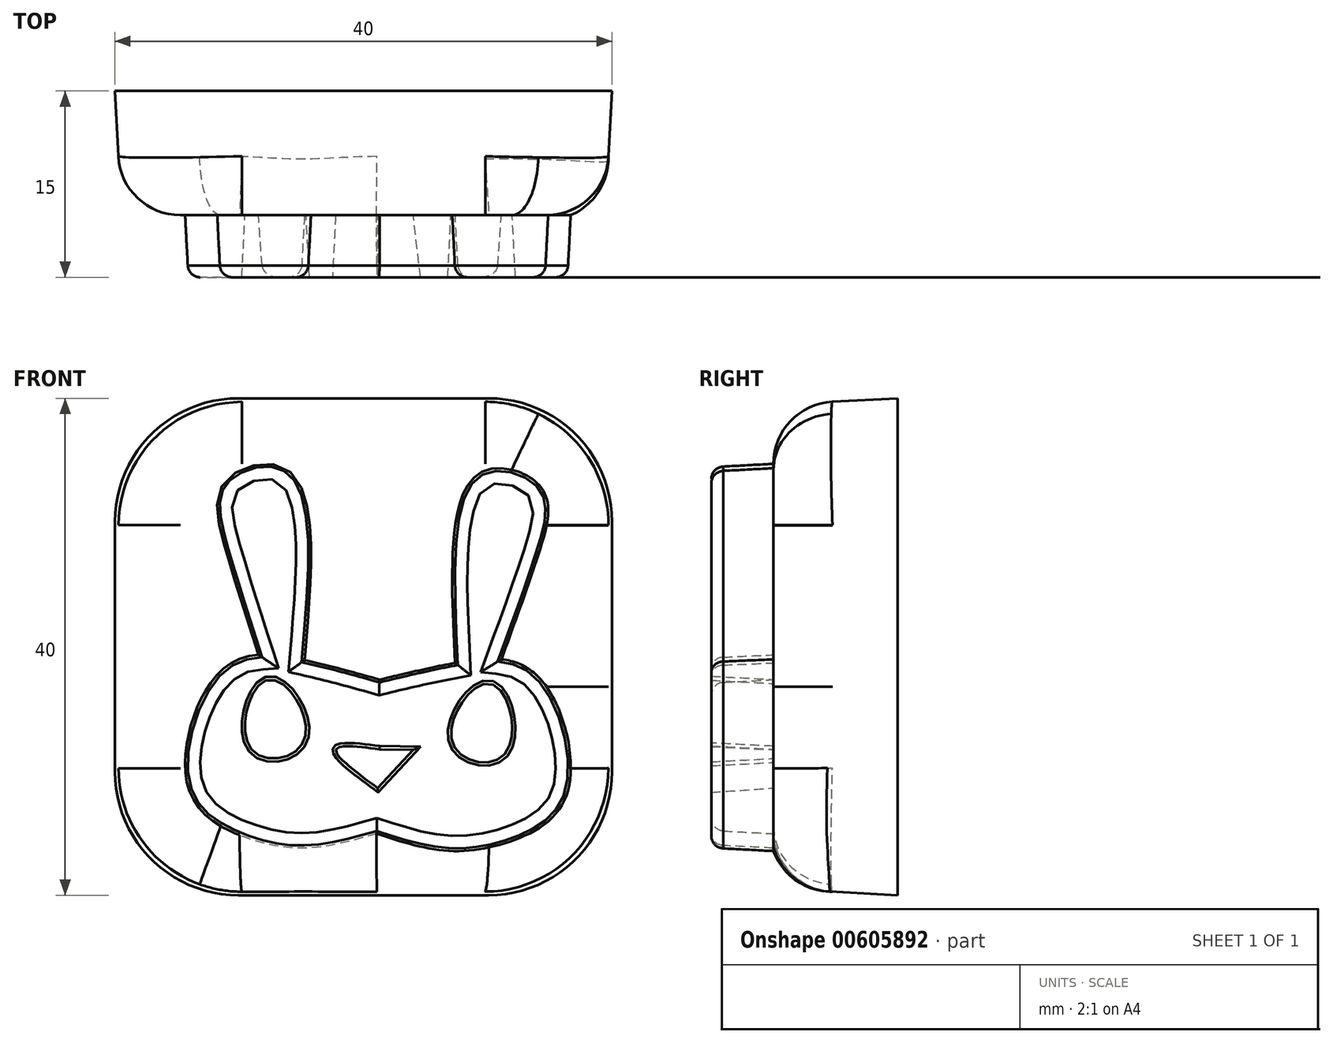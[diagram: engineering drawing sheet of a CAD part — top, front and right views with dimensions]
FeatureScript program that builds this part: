
annotation { "Feature Type Name" : "Feature", "Feature Type Description" : "" }
export const myFeature = defineFeature(function(context is Context, id is Id, definition is map)
    precondition{}
    {
        {
            var Q0;
            Q0=qCreatedBy(makeId("Front.planeOp"),FACE);
            var sketch = newSketch(context, id + "F0", { "sketchPlane" : qUnion([Q0])});
            skLineSegment(sketch, "E0.bottom", {"start": v(-5.85, 16.71) * mm, "end": v(34.15, 16.71) * mm});
            skLineSegment(sketch, "E0.top", {"start": v(-5.85, -23.29) * mm, "end": v(34.15, -23.29) * mm});
            skLineSegment(sketch, "E0.left", {"start": v(-5.85, 16.71) * mm, "end": v(-5.85, -23.29) * mm});
            skLineSegment(sketch, "E0.right", {"start": v(34.15, 16.71) * mm, "end": v(34.15, -23.29) * mm});
            skSolve(sketch);
        }
        {
            var Q0;
            Q0=makeQuery(id+"F0.imprint","IMPRINT",FACE,{"disambiguationData":[TD([[makeQuery(id+"F0.imprint","IMPRINT",EDGE,{"derivedFrom":sQuery(id+"F0.wireOp",EDGE,"E0.bottom")}),-1.0]])]});
            extrude(context, id + "F1", {"entities" : qUnion([Q0]), "depth" : 10 * mm, "offsetDistance" : 25 * mm, "hasDraft" : true, "draftAngle" : 3 * degree, "draftPullDirection" : true});
        }
        {
            var Q0;
            Q0=makeQuery(id+"F1.opExtrude","CAP_FACE",FACE,{"disambiguationData":[OSD([sQuery(id+"F0.wireOp",EDGE,"E0.bottom"),sQuery(id+"F0.wireOp",EDGE,"E0.top"),sQuery(id+"F0.wireOp",EDGE,"E0.left"),sQuery(id+"F0.wireOp",EDGE,"E0.right")])],"isStart":false});
            var sketch = newSketch(context, id + "F2", { "sketchPlane" : qUnion([Q0])});
            skFitSpline(sketch, "E1", {"points": [v(15.44, -5.94) * mm, v(9.4, -4.36) * mm, v(3, -4.95) * mm, v(0, -14.45) * mm, v(4.36, -18.52) * mm, v(9.6, -19.5) * mm, v(15.21, -18.34) * mm], "startDerivative": vector(-35.84, 10.1) * mm, "endDerivative": vector(36.32, 10.37) * mm});
            skFitSpline(sketch, "E2", {"points": [v(5.7, -3.94) * mm, v(3, 4.75) * mm, v(3, 9.99) * mm, v(8.05, 10.96) * mm, v(9.4, -4.36) * mm], "startDerivative": vector(-11.04, 34.2) * mm, "endDerivative": vector(-5.26, -59.75) * mm});
            skFitSpline(sketch, "E3", {"points": [v(6.5, -5.94) * mm, v(5.14, -11.54) * mm, v(9.4, -10.77) * mm, v(6.5, -5.94) * mm]});
            skFitSpline(sketch, "E4", {"points": [v(15.44, -11.54) * mm, v(11.93, -11.54) * mm, v(15.28, -14.66) * mm], "startDerivative": vector(-10.75, 1.37) * mm, "endDerivative": vector(9.97, -7.41) * mm});
            skFitSpline(sketch, "E5.MirrorCS", {"points": [v(25.25, -4.3) * mm, v(28.27, 4.28) * mm, v(28.46, 9.51) * mm, v(23.46, 10.67) * mm, v(21.53, -4.6) * mm], "startDerivative": vector(12.3, 33.76) * mm, "endDerivative": vector(3.03, -59.9) * mm});
            skFitSpline(sketch, "E6.MirrorCS", {"points": [v(15.44, -5.94) * mm, v(21.53, -4.6) * mm, v(27.9, -5.41) * mm, v(30.56, -15.02) * mm, v(26.04, -18.93) * mm, v(20.78, -19.7) * mm, v(15.21, -18.34) * mm], "startDerivative": vector(36.2, 8.75) * mm, "endDerivative": vector(-35.9, 11.72) * mm});
            skFitSpline(sketch, "E7.MirrorC", {"points": [v(24.38, -6.27) * mm, v(25.53, -11.92) * mm, v(21.3, -10.99) * mm, v(24.38, -6.27) * mm]});
            skLineSegment(sketch, "E8", {"start": v(15.44, -11.54) * mm, "end": v(18.15, -11.6) * mm});
            skLineSegment(sketch, "E9", {"start": v(18.15, -11.6) * mm, "end": v(15.28, -14.66) * mm});
            skSolve(sketch);
        }
        {
            var Q0;
            Q0 = qSketchRegion(id + "F2", true);
            extrude(context, id + "F3", {"entities" : qUnion([Q0]), "operationType" : NewBodyOperationType.ADD, "depth" : 5 * mm, "offsetDistance" : 25 * mm, "hasDraft" : true, "draftAngle" : 3 * degree, "draftPullDirection" : true});
        }
        {
            var Q0;
            Q0=makeQuery(id+"F1.opExtrude","SWEPT_EDGE",EDGE,{"disambiguationData":[OSD([sQuery(id+"F0.wireOp",EDGE,"E0.bottom"),sQuery(id+"F0.wireOp",EDGE,"E0.left")])]});
            var Q1;
            Q1=makeQuery(id+"F1.opExtrude","SWEPT_EDGE",EDGE,{"disambiguationData":[OSD([sQuery(id+"F0.wireOp",EDGE,"E0.bottom"),sQuery(id+"F0.wireOp",EDGE,"E0.right")])]});
            var Q2;
            Q2=makeQuery(id+"F1.opExtrude","SWEPT_EDGE",EDGE,{"disambiguationData":[OSD([sQuery(id+"F0.wireOp",EDGE,"E0.top"),sQuery(id+"F0.wireOp",EDGE,"E0.right")])]});
            var Q3;
            Q3=makeQuery(id+"F1.opExtrude","SWEPT_EDGE",EDGE,{"disambiguationData":[OSD([sQuery(id+"F0.wireOp",EDGE,"E0.top"),sQuery(id+"F0.wireOp",EDGE,"E0.left")])]});
            fillet(context, id + "F4", {"entities" : qUnion([Q0, Q1, Q2, Q3]), "radius" : 9.94 * mm, "tangentPropagation" : true, "allowEdgeOverflow" : false});
        }
        {
            var Q0;
            {var subQ0=sQuery(id+"F0.wireOp",EDGE,"E0.left");var subQ1=sQuery(id+"F0.wireOp",EDGE,"E0.top");var subQ2=sQuery(id+"F0.wireOp",EDGE,"E0.right");var subQ7=sQuery(id+"F0.wireOp",EDGE,"E0.bottom");Q0=makeQuery(id+"F4.opFillet","BLEND_EDGE",EDGE,{"blendedFrom":[makeQuery(id+"F1.opExtrude","SWEPT_EDGE",EDGE,{"disambiguationData":[OSD([subQ1,subQ0])]}),makeQuery(id+"F3.boolean.opBoolean","SPLIT",FACE,{"disambiguationData":[TD([makeQuery(id+"F1.opExtrude","SWEPT_FACE",FACE,{"disambiguationData":[OSD([subQ7])]})])],"derivedFrom":makeQuery(id+"F1.opExtrude","CAP_FACE",FACE,{"disambiguationData":[OSD([subQ7,subQ1,subQ0,subQ2])],"isStart":false})})],"blendedInto":[makeQuery(id+"F3.boolean.opBoolean","SPLIT",FACE,{"disambiguationData":[TD([makeQuery(id+"F1.opExtrude","SWEPT_FACE",FACE,{"disambiguationData":[OSD([subQ7])]})])],"derivedFrom":makeQuery(id+"F1.opExtrude","CAP_FACE",FACE,{"disambiguationData":[OSD([subQ7,subQ1,subQ0,subQ2])],"isStart":false})})]});}
            var Q1;
            Q1=makeQuery(id+"F1.opExtrude","CAP_EDGE",EDGE,{"disambiguationData":[OSD([sQuery(id+"F0.wireOp",EDGE,"E0.top")])],"isStart":false});
            fillet(context, id + "F5", {"entities" : qUnion([Q0, Q1]), "radius" : 5 * mm, "tangentPropagation" : true, "allowEdgeOverflow" : false});
        }
        {
            var Q0;
            Q0=makeQuery(id+"F3.opExtrude","CAP_EDGE",EDGE,{"disambiguationData":[OSD([sQuery(id+"F2.wireOp",EDGE,"E2")])],"isStart":false});
            var Q1;
            {var subQ0=sQuery(id+"F2.wireOp",EDGE,"E1");Q1=makeQuery(id+"F3.opExtrude","CAP_EDGE",EDGE,{"disambiguationData":[OSD([subQ0]),TDD([makeQuery(id+"F2.imprint","IMPRINT",EDGE,{"disambiguationData":[TD([[makeQuery(id+"F2.imprint","INTERSECT",VERTEX,{"disambiguationData":[OD(1.0)],"derivedFrom":[subQ0,sQuery(id+"F2.wireOp",EDGE,"E6.MirrorCS")]}),1.0]])],"derivedFrom":subQ0})])],"isStart":false});}
            var Q2;
            {var subQ0=sQuery(id+"F2.wireOp",EDGE,"E1");Q2=makeQuery(id+"F3.opExtrude","CAP_EDGE",EDGE,{"disambiguationData":[OSD([subQ0]),TDD([makeQuery(id+"F2.imprint","IMPRINT",EDGE,{"disambiguationData":[TD([[makeQuery(id+"F2.imprint","INTERSECT",VERTEX,{"disambiguationData":[OD(0.0)],"derivedFrom":[subQ0,sQuery(id+"F2.wireOp",EDGE,"E6.MirrorCS")]}),-1.0]])],"derivedFrom":subQ0})])],"isStart":false});}
            var Q3;
            {var subQ0=sQuery(id+"F2.wireOp",EDGE,"E6.MirrorCS");Q3=makeQuery(id+"F3.opExtrude","CAP_EDGE",EDGE,{"disambiguationData":[OSD([subQ0]),TDD([makeQuery(id+"F2.imprint","IMPRINT",EDGE,{"disambiguationData":[TD([[makeQuery(id+"F2.imprint","INTERSECT",VERTEX,{"disambiguationData":[OD(0.0)],"derivedFrom":[sQuery(id+"F2.wireOp",EDGE,"E1"),subQ0]}),-1.0]])],"derivedFrom":subQ0})])],"isStart":false});}
            var Q4;
            Q4=makeQuery(id+"F3.opExtrude","CAP_EDGE",EDGE,{"disambiguationData":[OSD([sQuery(id+"F2.wireOp",EDGE,"E5.MirrorCS")])],"isStart":false});
            var Q5;
            {var subQ0=sQuery(id+"F2.wireOp",EDGE,"E6.MirrorCS");Q5=makeQuery(id+"F3.opExtrude","CAP_EDGE",EDGE,{"disambiguationData":[OSD([subQ0]),TDD([makeQuery(id+"F2.imprint","IMPRINT",EDGE,{"disambiguationData":[TD([[makeQuery(id+"F2.imprint","INTERSECT",VERTEX,{"disambiguationData":[OD(1.0)],"derivedFrom":[sQuery(id+"F2.wireOp",EDGE,"E1"),subQ0]}),1.0]])],"derivedFrom":subQ0})])],"isStart":false});}
            fillet(context, id + "F6", {"entities" : qUnion([Q0, Q1, Q2, Q3, Q4, Q5]), "radius" : 1 * mm, "tangentPropagation" : true, "allowEdgeOverflow" : false});
        }
    });
